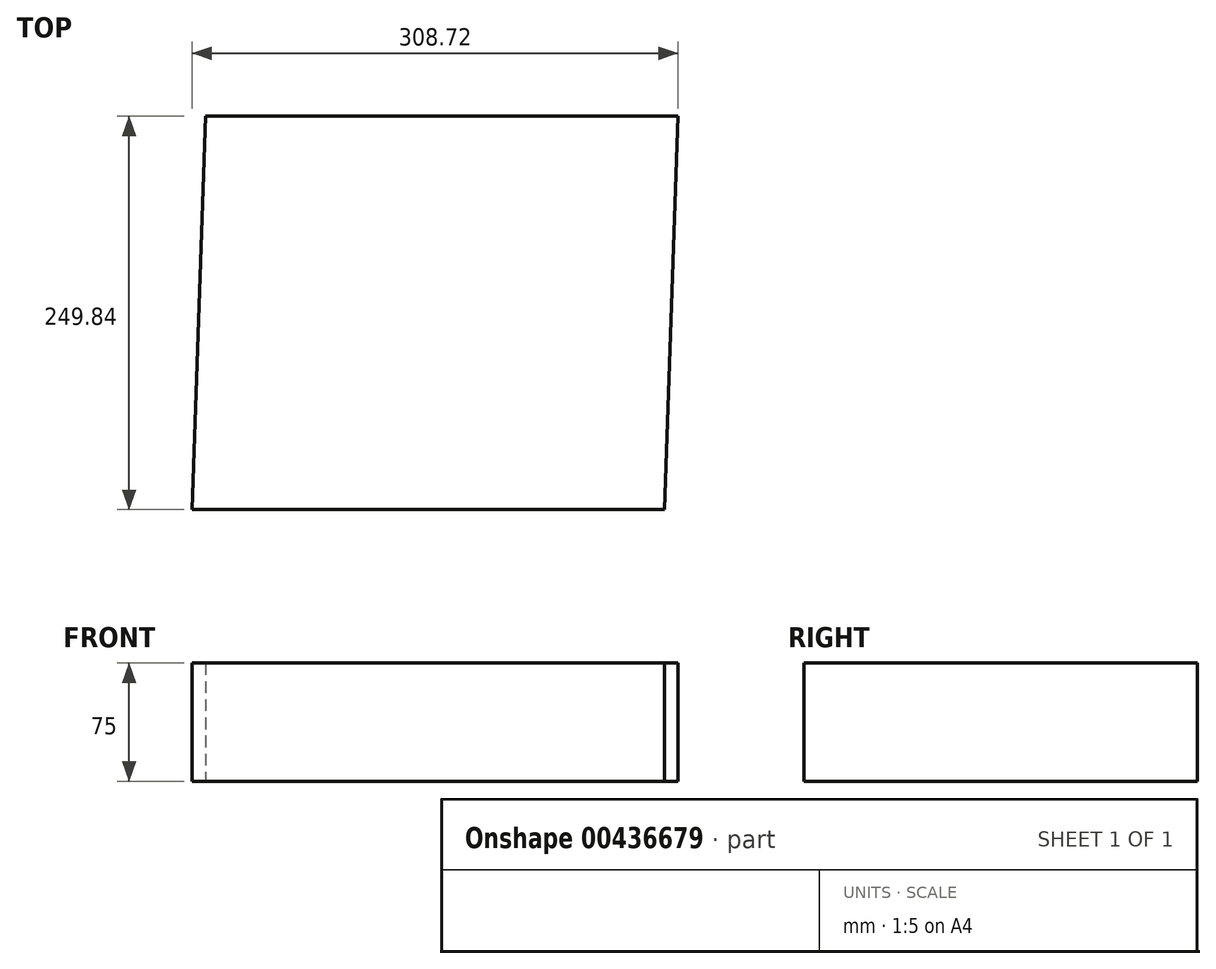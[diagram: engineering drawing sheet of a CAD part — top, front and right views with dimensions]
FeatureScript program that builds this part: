
annotation { "Feature Type Name" : "Feature", "Feature Type Description" : "" }
export const myFeature = defineFeature(function(context is Context, id is Id, definition is map)
    precondition{}
    {
        {
            var Q0;
            Q0=qCreatedBy(makeId("Top.planeOp"),FACE);
            var sketch = newSketch(context, id + "F0", { "sketchPlane" : qUnion([Q0])});
            skLineSegment(sketch, "E0.bottom", {"start": v(145.64, -124.92) * mm, "end": v(-154.36, -124.92) * mm});
            skLineSegment(sketch, "E0.top", {"start": v(154.36, 124.92) * mm, "end": v(-145.64, 124.92) * mm});
            skLineSegment(sketch, "E0.left", {"start": v(145.64, -124.92) * mm, "end": v(154.36, 124.92) * mm});
            skLineSegment(sketch, "E0.right", {"start": v(-154.36, -124.92) * mm, "end": v(-145.64, 124.92) * mm});
            skPoint(sketch, "E0.middle", {"position": v(0, 0) * mm});
            skSolve(sketch);
        }
        {
            var Q0;
            Q0=qSketchRegion(id+"F0",true);
            extrude(context, id + "F1", {"entities" : qUnion([Q0]), "depth" : 75 * mm});
        }
    });
